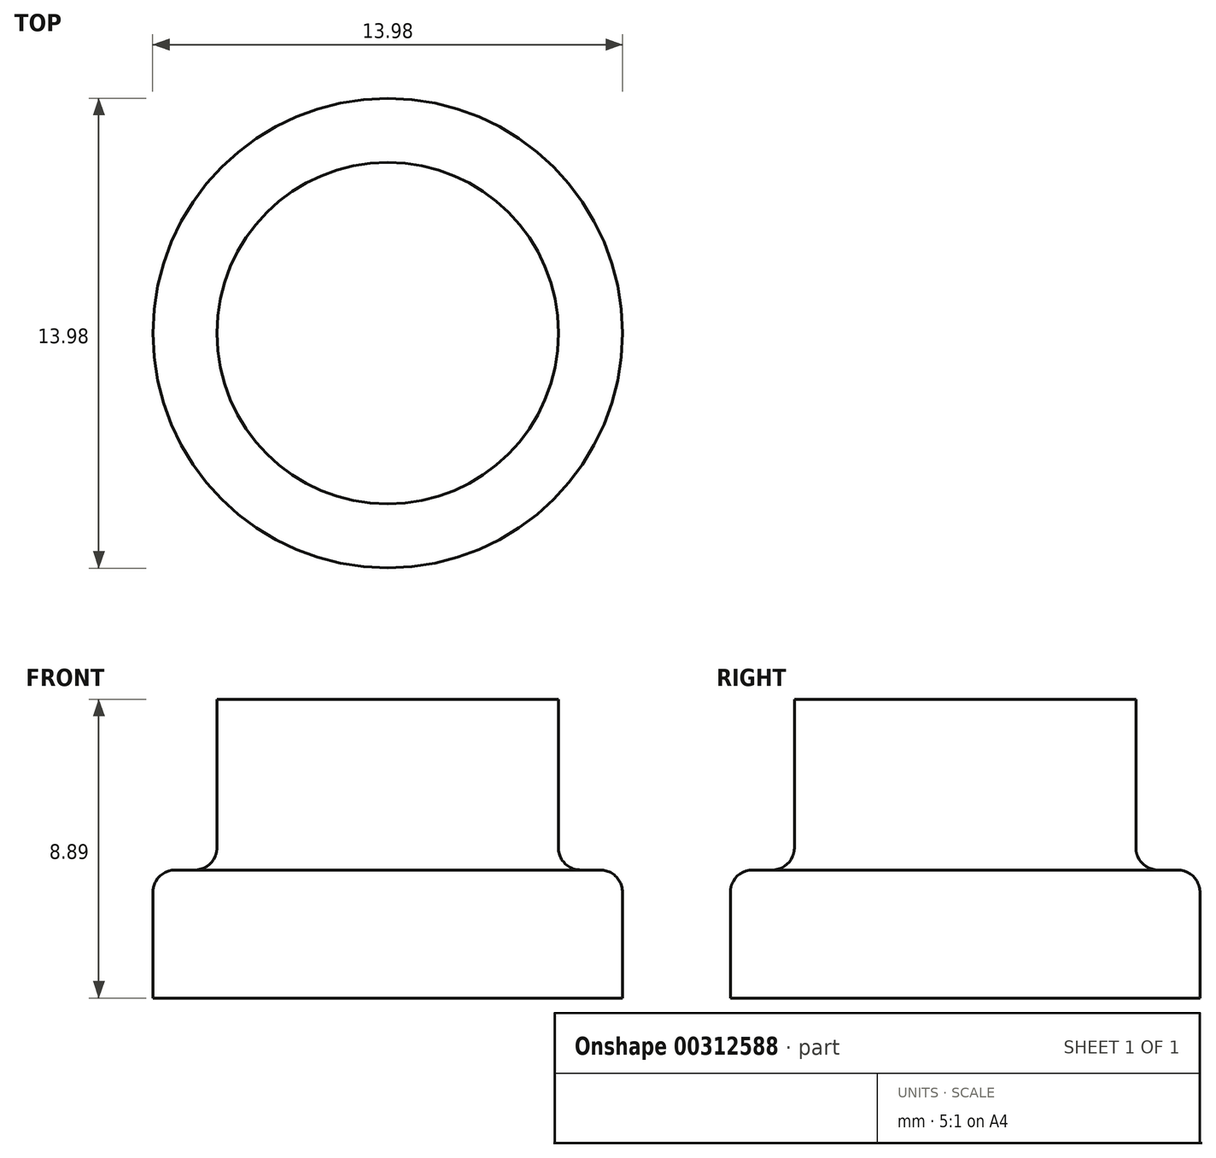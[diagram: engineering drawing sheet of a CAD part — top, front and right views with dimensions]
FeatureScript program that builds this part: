
annotation { "Feature Type Name" : "Feature", "Feature Type Description" : "" }
export const myFeature = defineFeature(function(context is Context, id is Id, definition is map)
    precondition{}
    {
        {
            var Q0;
            Q0=qCreatedBy(makeId("Top.planeOp"),FACE);
            var sketch = newSketch(context, id + "F0", { "sketchPlane" : qUnion([Q0])});
            skCircle(sketch, "E0", {"center": v(0, 0) * mm, "radius": 5.08 * mm});
            skCircle(sketch, "E1", {"center": v(0, 0) * mm, "radius": 6.99 * mm});
            skSolve(sketch);
        }
        {
            var Q0;
            Q0=makeQuery(id+"F0.imprint","IMPRINT",FACE,{"disambiguationData":[TD([[makeQuery(id+"F0.imprint","IMPRINT",EDGE,{"derivedFrom":sQuery(id+"F0.wireOp",EDGE,"E0")}),1.0]])]});
            var Q1;
            Q1=sQuery(id+"F0.wireOp",EDGE,"E0");
            extrude(context, id + "F1", {"entities" : qUnion([Q0]), "surfaceEntities" : qUnion([Q1]), "depth" : 8.9 * mm});
        }
        {
            var Q0;
            Q0=makeQuery(id+"F0.imprint","IMPRINT",FACE,{"disambiguationData":[TD([[makeQuery(id+"F0.imprint","IMPRINT",EDGE,{"derivedFrom":sQuery(id+"F0.wireOp",EDGE,"E0")}),-1.0]])]});
            extrude(context, id + "F2", {"entities" : qUnion([Q0]), "operationType" : NewBodyOperationType.ADD, "depth" : 3.8 * mm});
        }
        {
            var Q0;
            Q0=makeQuery(id+"F2.opExtrude","CAP_FACE",FACE,{"disambiguationData":[OSD([sQuery(id+"F0.wireOp",EDGE,"E0"),sQuery(id+"F0.wireOp",EDGE,"E1")])],"isStart":false});
            fillet(context, id + "F3", {"entities" : qUnion([Q0]), "radius" : 0.66 * mm, "tangentPropagation" : true, "allowEdgeOverflow" : false});
        }
    });
